# Revit family: Interceptor_Oil-Zurn-Z1198-ST
name_source: partatom
category: Plumbing Fixtures
units: mm (PartAtom-declared; Revit-internal decimal feet)

## family parameters
Always vertical = Yes
Cut with Voids When Loaded = No
Maintain Annotation Orientation = No
OmniClass Number = 23.45.30.00
OmniClass Title = Washing and Waste Disposal Equipment
Part Type = Normal
Room Calculation Point = No
Round Connector Dimension = Use Radius
Shared = No
Work Plane-Based = No

## types (1)
- Load Family Type Catalog
    Approx. Weight (Lbs) = 5500.00 lb
    Assembly Code = D2090300
    C = 57.25 "
    CW Connection = No
    CWFU = 0
    D/E = 51.625 "
    Default Elevation = 20 "
    Description = LARGE CAPACITY OIL INTERCEPTOR W/ INTEGRAL STORAGE TANK & OIL LEVEL FLOAT SENSOR
    F = 124.125 "
    G = 103.625 "
    H = 73.938 "
    HW Connection = No
    HWFU = 0
    J = 48.125 "
    Main Material = Steel - Zurn - Fabricated - Acid resistant Coated
    Manufacturer = Zurn Water, LLC
    Manufacturer Brand = Zurn
    Model = Z1198-ST
    Modified Date = 02/20/2026
    Oil Storage Tank Capacity (Gal) = 700.00 L
    Pipe Size Inside Radius = 3.033 "
    Pipe Size Nominal Radius = 3 "
    Pipe Size Outer Radius = 3.313 "
    Product Documentation Link = https://files.zurn.com
    Product Installation Sheet URL = https://files.zurn.com
    Product Page URL = https://www.zurn.com
    Product data URL = https://www.bimobject.com
    Type Comments = Z1198-ST-500 GPM with 6 Inch Inlet/ outlet
    URL = www.zurn.com
    Vent Connection = No
    WFU = 1
    Waste Connection = Yes
    Water Capacity (Gal) = 1695.00 L
    Width of Interceptor = 37 "

## geometry (parser evidence)
native form markers: Sweep x3
no freeform markers — native parametric forms only
